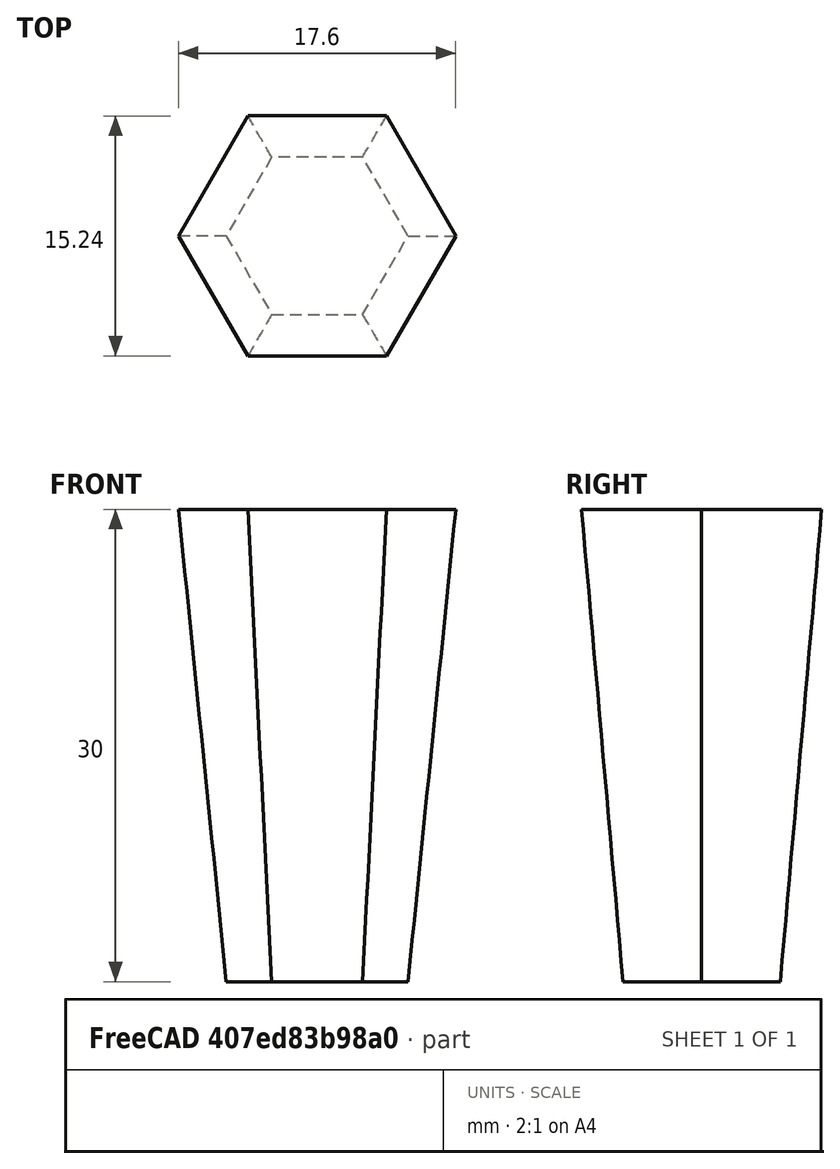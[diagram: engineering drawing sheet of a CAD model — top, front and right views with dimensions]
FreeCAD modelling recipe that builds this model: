
FCSTD DOCUMENT  (FreeCAD 0.17RUnknown)
Label: test105_blinderthing
License: All rights reserved
LicenseURL: http://en.wikipedia.org/wiki/All_rights_reserved
objects: Mesh::Feature×1, PartDesign::Plane×1, Sketcher::SketchObject×1, Part::Extrusion×1, PartDesign::Body×1
note: 4 computed .brp shape members not serialized (recipe doc carries the construction recipe); baked Part::Feature solids carry a one-line shape summary decoded from their .brp

FEATURE [Mesh::Feature] test105_blinderthing
FEATURE [PartDesign::Plane] DatumPlane
  AttachmentOffset = pos=(0,0,10) rot=(0,0,1;0rad)
  MapMode = 5
  Placement = pos=(0,0,10) rot=(0,0,1;0rad)
  Support = -> [XY_Plane]
FEATURE [Sketcher::SketchObject] Sketch
  MapMode = 5
  Placement = pos=(0,0,10) rot=(0,0,1;0rad)
  Support = -> [DatumPlane]
  sketch-geometry (14):
    g0: LineSegment [constr] StartX=0 StartY=0 StartZ=0 EndX=5.7 EndY=0 EndZ=0
    g1: LineSegment [constr] StartX=5.7 StartY=0 StartZ=0 EndX=5.7 EndY=5.7 EndZ=0
    g2: LineSegment [constr] StartX=5.7 StartY=5.7 StartZ=0 EndX=0 EndY=5.7 EndZ=0
    g3: LineSegment [constr] StartX=0 StartY=5.7 StartZ=0 EndX=0 EndY=0 EndZ=0
    g4: LineSegment [constr] StartX=0 StartY=5.7 StartZ=0 EndX=5.7 EndY=0 EndZ=0
    g5: LineSegment [constr] StartX=0 StartY=0 StartZ=0 EndX=5.7 EndY=5.7 EndZ=0
    g6: GeomPoint X=2.85 Y=2.85 Z=0
    g7: LineSegment StartX=8.6235 StartY=2.85 StartZ=0 EndX=5.73675 EndY=7.85 EndZ=0
    g8: LineSegment StartX=5.73675 StartY=7.85 StartZ=0 EndX=-0.0367513 EndY=7.85 EndZ=0
    g9: LineSegment StartX=-0.0367513 StartY=7.85 StartZ=0 EndX=-2.9235 EndY=2.85 EndZ=0
    g10: LineSegment StartX=-2.9235 StartY=2.85 StartZ=0 EndX=-0.0367513 EndY=-2.15 EndZ=0
    g11: LineSegment StartX=-0.0367513 StartY=-2.15 StartZ=0 EndX=5.73675 EndY=-2.15 EndZ=0
    g12: LineSegment StartX=5.73675 StartY=-2.15 StartZ=0 EndX=8.6235 EndY=2.85 EndZ=0
    g13: Circle [constr] CenterX=2.85 CenterY=2.85 CenterZ=0 NormalX=0 NormalY=0 NormalZ=1 AngleXU=0 Radius=5.7735
  constraints (33):
    c: Coincident(g0,g1)
    c: Coincident(g1,g2)
    c: Coincident(g2,g3)
    c: Coincident(g3,g0)
    c: Horizontal(g0)
    c: Horizontal(g2)
    c: Vertical(g1)
    c: Vertical(g3)
    c: Coincident(g0,g-1)
    c: DistanceY(g1,g1) = 5.7
    c: DistanceX(g2,g2) = 5.7
    c: Coincident(g4,g2)
    c: Coincident(g4,g0)
    c: Coincident(g5,g1)
    c: PointOnObject(g6,g4)
    c: PointOnObject(g6,g5)
    c: Coincident(g7,g8)
    c: Coincident(g8,g9)
    c: Coincident(g9,g10)
    c: Coincident(g10,g11)
    c: Coincident(g11,g12)
    c: Coincident(g12,g7)
    c: Equal(g7, g8-g12) x5
    c: PointOnObject(g7,g13)
    c: PointOnObject(g8,g13)
    c: PointOnObject(g9,g13)
    c: PointOnObject(g10,g13)
    c: PointOnObject(g11,g13)
    c: PointOnObject(g12,g13)
    c: Coincident(g13,g6)
    c: Distance(g6,g7) = 5
    c: Horizontal(g11)
    c: Coincident(g5,g-1)
FEATURE [Part::Extrusion] Extrude
  Base = -> Sketch
  Dir = (0,0,1)
  DirMode = 2
  FaceMakerClass = Part::FaceMakerBullseye
  LengthFwd = 30
  LengthRev = 0
  Solid = true
  Symmetric = false
  TaperAngle = 5
FEATURE [PartDesign::Body] Body
  Group = -> [DatumPlane,Sketch]
  Origin = -> Origin
